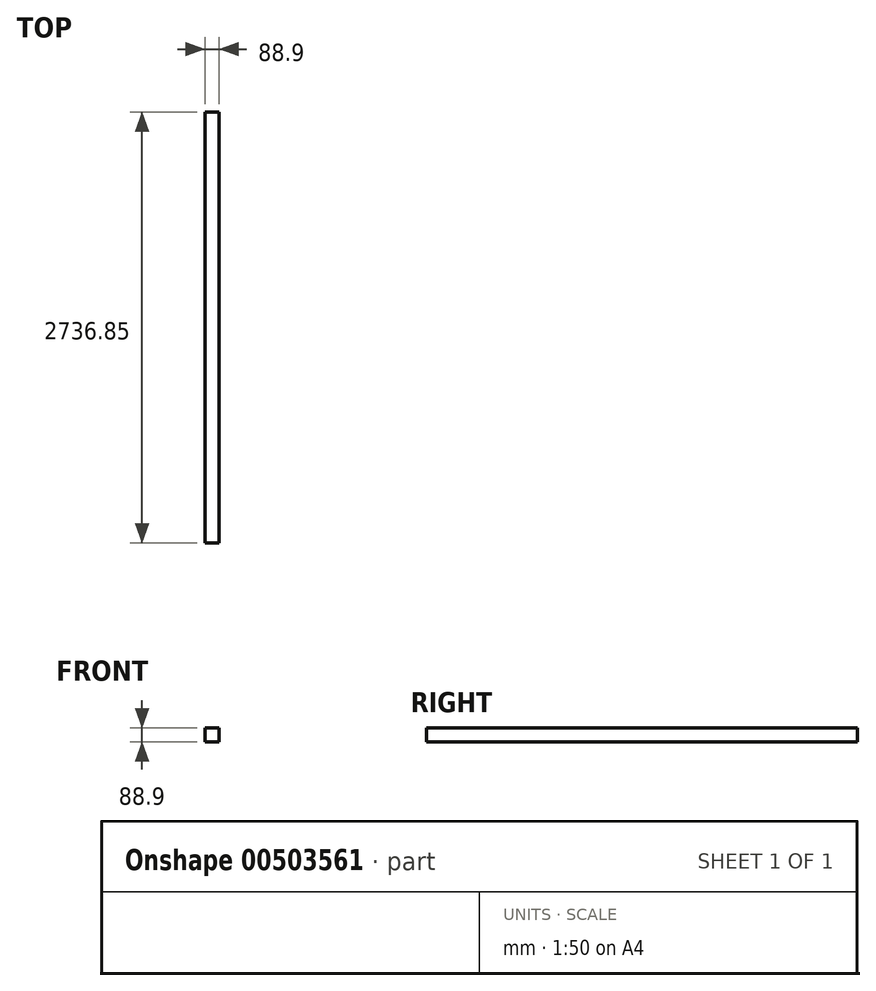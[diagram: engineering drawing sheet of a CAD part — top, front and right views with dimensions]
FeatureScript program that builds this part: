
annotation { "Feature Type Name" : "Feature", "Feature Type Description" : "" }
export const myFeature = defineFeature(function(context is Context, id is Id, definition is map)
    precondition{}
    {
        {
            var Q0;
            Q0=qCreatedBy(makeId("Front.planeOp"),FACE);
            var sketch = newSketch(context, id + "F0", { "sketchPlane" : qUnion([Q0])});
            skLineSegment(sketch, "E0.bottom", {"start": v(0, 0) * mm, "end": v(88.9, 0) * mm});
            skLineSegment(sketch, "E0.top", {"start": v(0, 88.9) * mm, "end": v(88.9, 88.9) * mm});
            skLineSegment(sketch, "E0.left", {"start": v(0, 0) * mm, "end": v(0, 88.9) * mm});
            skLineSegment(sketch, "E0.right", {"start": v(88.9, 0) * mm, "end": v(88.9, 88.9) * mm});
            skSolve(sketch);
        }
        {
            var Q0;
            Q0 = qSketchRegion(id + "F0", true);
            extrude(context, id + "F1", {"entities" : qUnion([Q0]), "depth" : 2736.85 * mm});
        }
    });
